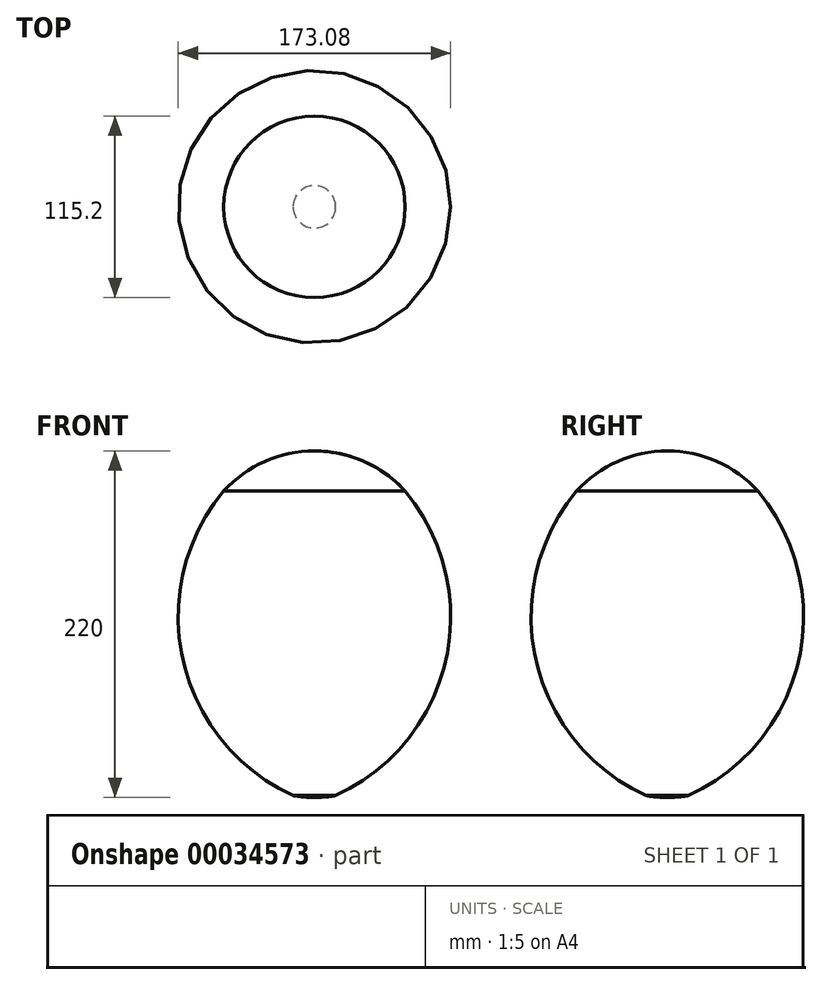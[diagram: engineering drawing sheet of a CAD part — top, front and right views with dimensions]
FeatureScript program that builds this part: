
annotation { "Feature Type Name" : "Feature", "Feature Type Description" : "" }
export const myFeature = defineFeature(function(context is Context, id is Id, definition is map)
    precondition{}
    {
        {
            var Q0;
            Q0=qCreatedBy(makeId("Front.planeOp"),FACE);
            var sketch = newSketch(context, id + "F0", { "sketchPlane" : qUnion([Q0])});
            skLineSegment(sketch, "E0", {"start": v(0, 0) * mm, "end": v(-85, 0) * mm, "construction": true});
            skLineSegment(sketch, "E1", {"start": v(0, 0) * mm, "end": v(0, -95.17) * mm, "construction": true});
            skLineSegment(sketch, "E2", {"start": v(0, 0) * mm, "end": v(0, 138.3) * mm, "construction": true});
            skLineSegment(sketch, "E3", {"start": v(0, 124.83) * mm, "end": v(0, -95.17) * mm});
            skArc(sketch, "E4", {"start": v(-57.6, 99.43) * mm, "mid": v(-83.42, -8.2) * mm, "end": v(-13.52, -94) * mm});
            skArc(sketch, "E5", {"start": v(0, 124.83) * mm, "mid": v(-31.48, 118.2) * mm, "end": v(-57.6, 99.43) * mm});
            skArc(sketch, "E6", {"start": v(-13.52, -94) * mm, "mid": v(-6.79, -94.88) * mm, "end": v(0, -95.17) * mm});
            skSolve(sketch);
        }
        {
            var Q0;
            Q0=makeQuery(id+"F0.imprint","IMPRINT",FACE,{"disambiguationData":[TD([[makeQuery(id+"F0.imprint","IMPRINT",EDGE,{"derivedFrom":sQuery(id+"F0.wireOp",EDGE,"E3")}),-1.0]])]});
            var Q1;
            Q1=sQuery(id+"F0.wireOp",EDGE,"E3");
            revolve(context, id + "F1", {"entities" : qUnion([Q0]), "axis" : qUnion([Q1]), "revolveType" : RevolveType.FULL});
        }
    });
